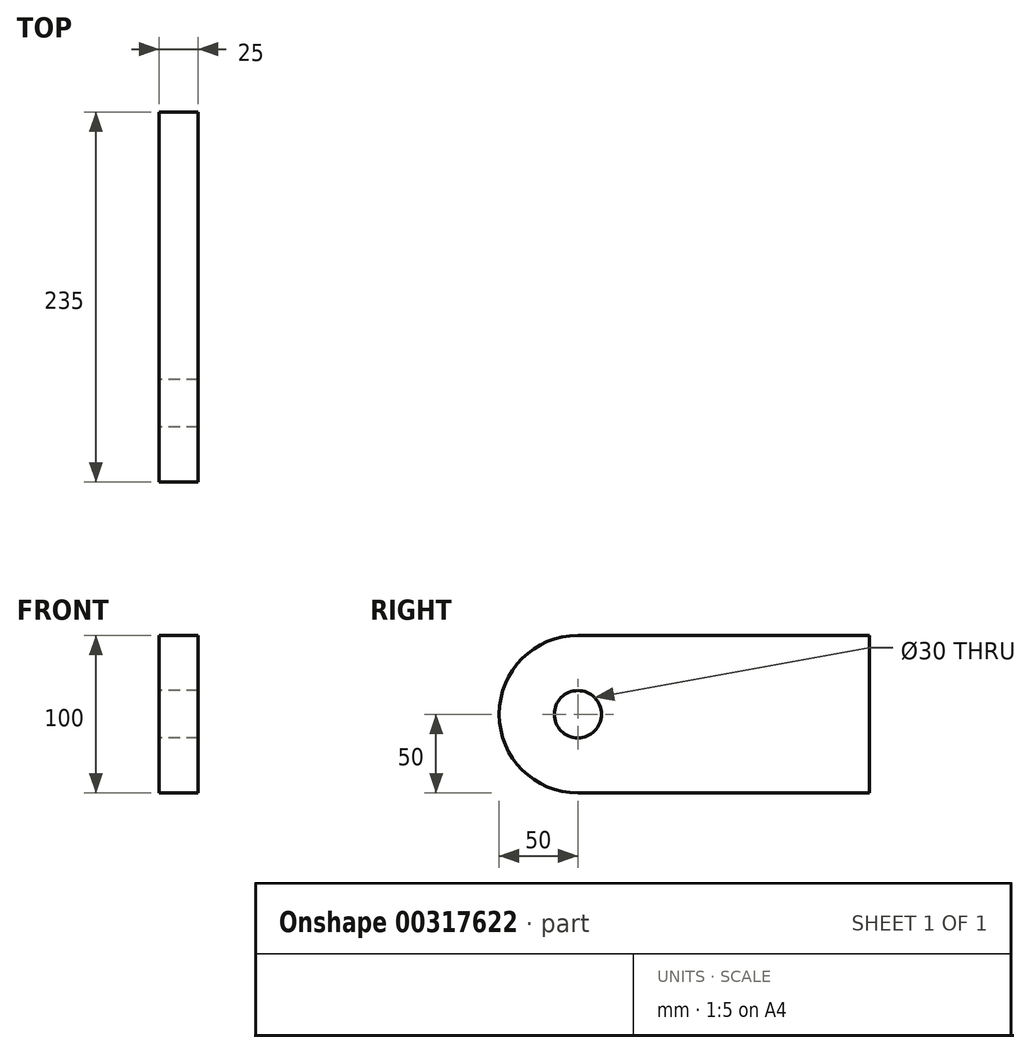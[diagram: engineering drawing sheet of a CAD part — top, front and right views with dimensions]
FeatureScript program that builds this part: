
annotation { "Feature Type Name" : "Feature", "Feature Type Description" : "" }
export const myFeature = defineFeature(function(context is Context, id is Id, definition is map)
    precondition{}
    {
        {
            var Q0;
            Q0=qCreatedBy(makeId("Right.planeOp"),FACE);
            var sketch = newSketch(context, id + "F0", { "sketchPlane" : qUnion([Q0])});
            skLineSegment(sketch, "E0.bottom", {"start": v(-50, 50) * mm, "end": v(185, 50) * mm});
            skLineSegment(sketch, "E0.top", {"start": v(-50, -50) * mm, "end": v(185, -50) * mm});
            skLineSegment(sketch, "E0.left", {"start": v(-50, 50) * mm, "end": v(-50, -50) * mm});
            skLineSegment(sketch, "E0.right", {"start": v(185, 50) * mm, "end": v(185, -50) * mm});
            skCircle(sketch, "E1", {"center": v(0, 0) * mm, "radius": 15 * mm});
            skSolve(sketch);
        }
        {
            var Q0;
            Q0 = qSketchRegion(id + "F0", true);
            extrude(context, id + "F1", {"entities" : qUnion([Q0]), "depth" : 25 * mm});
        }
        {
            var Q0;
            Q0=makeQuery(id+"F1.opExtrude","SWEPT_EDGE",EDGE,{"disambiguationData":[OSD([sQuery(id+"F0.wireOp",EDGE,"E0.bottom"),sQuery(id+"F0.wireOp",EDGE,"E0.left")])]});
            var Q1;
            Q1=makeQuery(id+"F1.opExtrude","SWEPT_EDGE",EDGE,{"disambiguationData":[OSD([sQuery(id+"F0.wireOp",EDGE,"E0.top"),sQuery(id+"F0.wireOp",EDGE,"E0.left")])]});
            fillet(context, id + "F2", {"entities" : qUnion([Q0, Q1]), "radius" : 50 * mm, "tangentPropagation" : true, "allowEdgeOverflow" : false});
        }
    });
